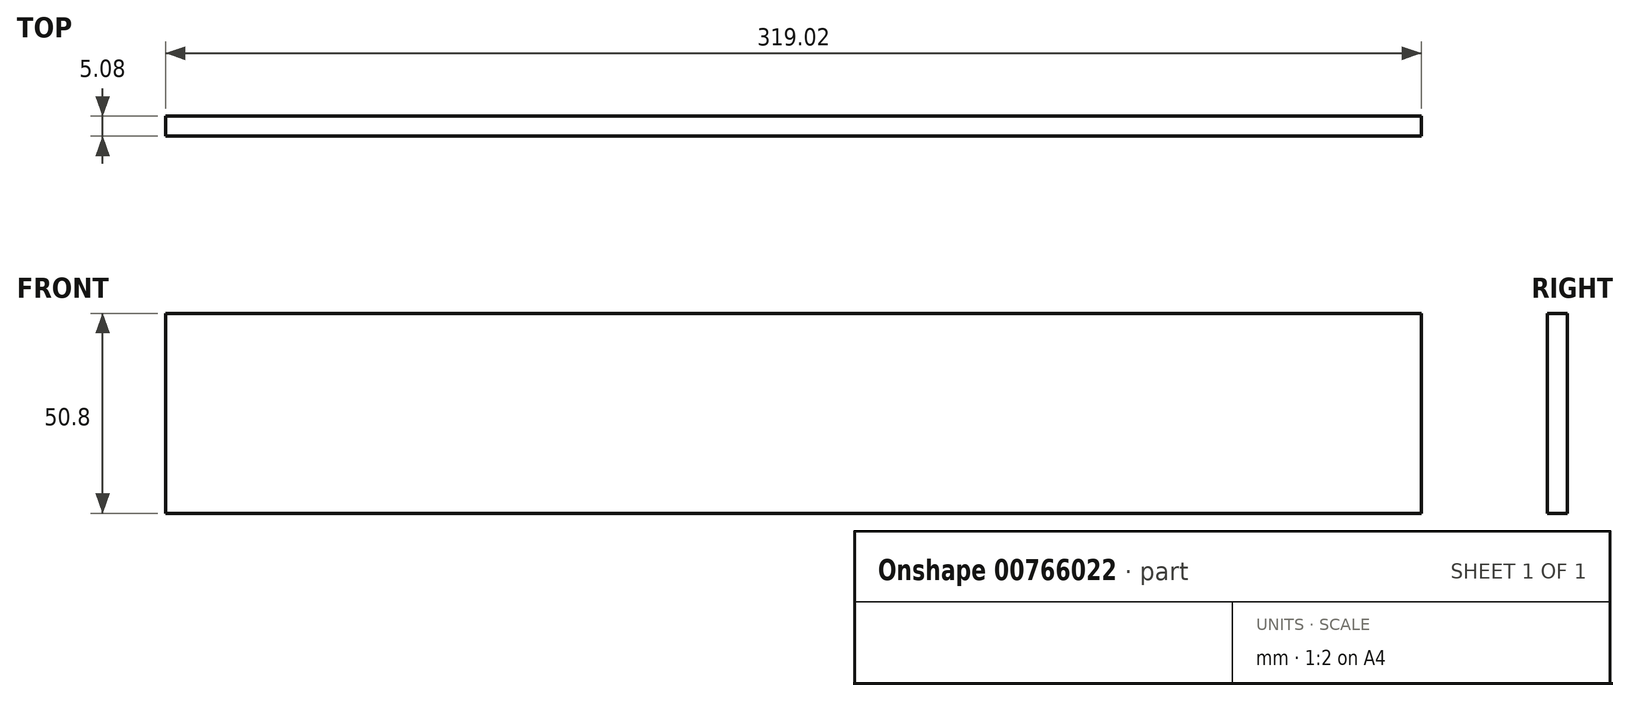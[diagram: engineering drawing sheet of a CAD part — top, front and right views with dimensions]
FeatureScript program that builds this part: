
annotation { "Feature Type Name" : "Feature", "Feature Type Description" : "" }
export const myFeature = defineFeature(function(context is Context, id is Id, definition is map)
    precondition{}
    {
        {
            var Q0;
            Q0=qCreatedBy(makeId("Front.planeOp"),FACE);
            var sketch = newSketch(context, id + "F0", { "sketchPlane" : qUnion([Q0])});
            skLineSegment(sketch, "E0", {"start": v(-87.9, 12.7) * mm, "end": v(-87.9, -38.1) * mm});
            skLineSegment(sketch, "E1", {"start": v(-87.9, -38.1) * mm, "end": v(231.12, -38.1) * mm});
            skLineSegment(sketch, "E2", {"start": v(231.12, -38.1) * mm, "end": v(231.12, 12.7) * mm});
            skLineSegment(sketch, "E3", {"start": v(231.12, 12.7) * mm, "end": v(-87.9, 12.7) * mm});
            skLineSegment(sketch, "E4", {"start": v(-75.2, 12.7) * mm, "end": v(-75.2, -38.1) * mm});
            skLineSegment(sketch, "E5", {"start": v(218.42, 12.7) * mm, "end": v(218.42, -38.1) * mm});
            skLineSegment(sketch, "E6", {"start": v(-87.9, 0) * mm, "end": v(-75.2, 0) * mm});
            skLineSegment(sketch, "E7", {"start": v(-75.2, 0) * mm, "end": v(-75.2, -12.7) * mm});
            skLineSegment(sketch, "E8", {"start": v(-75.2, -12.7) * mm, "end": v(-87.9, -12.7) * mm});
            skLineSegment(sketch, "E9", {"start": v(-87.9, -12.7) * mm, "end": v(-87.9, 0) * mm});
            skSolve(sketch);
        }
        {
            var Q0;
            {var subQ6=sQuery(id+"F0.wireOp",EDGE,"E5");Q0=makeQuery(id+"F0.imprint","IMPRINT",FACE,{"disambiguationData":[TD([[makeQuery(id+"F0.imprint","IMPRINT",EDGE,{"derivedFrom":subQ6}),-1.0]])]});}
            var Q1;
            {var subQ3=sQuery(id+"F0.wireOp",EDGE,"E8");Q1=makeQuery(id+"F0.imprint","IMPRINT",FACE,{"disambiguationData":[TD([[makeQuery(id+"F0.imprint","IMPRINT",EDGE,{"derivedFrom":subQ3}),1.0]])]});}
            var Q2;
            Q2=makeQuery(id+"F0.imprint","IMPRINT",FACE,{"disambiguationData":[TD([[makeQuery(id+"F0.imprint","IMPRINT",EDGE,{"derivedFrom":sQuery(id+"F0.wireOp",EDGE,"E6")}),-1.0]])]});
            var Q3;
            {var subQ3=sQuery(id+"F0.wireOp",EDGE,"E6");Q3=makeQuery(id+"F0.imprint","IMPRINT",FACE,{"disambiguationData":[TD([[makeQuery(id+"F0.imprint","IMPRINT",EDGE,{"derivedFrom":subQ3}),1.0]])]});}
            var Q4;
            {var subQ0=sQuery(id+"F0.wireOp",EDGE,"E2");Q4=makeQuery(id+"F0.imprint","IMPRINT",FACE,{"disambiguationData":[TD([[makeQuery(id+"F0.imprint","IMPRINT",EDGE,{"derivedFrom":subQ0}),1.0]])]});}
            extrude(context, id + "F1", {"entities" : qUnion([Q0, Q1, Q2, Q3, Q4]), "depth" : 5.08 * mm, "offsetDistance" : 25.4 * mm});
        }
    });
